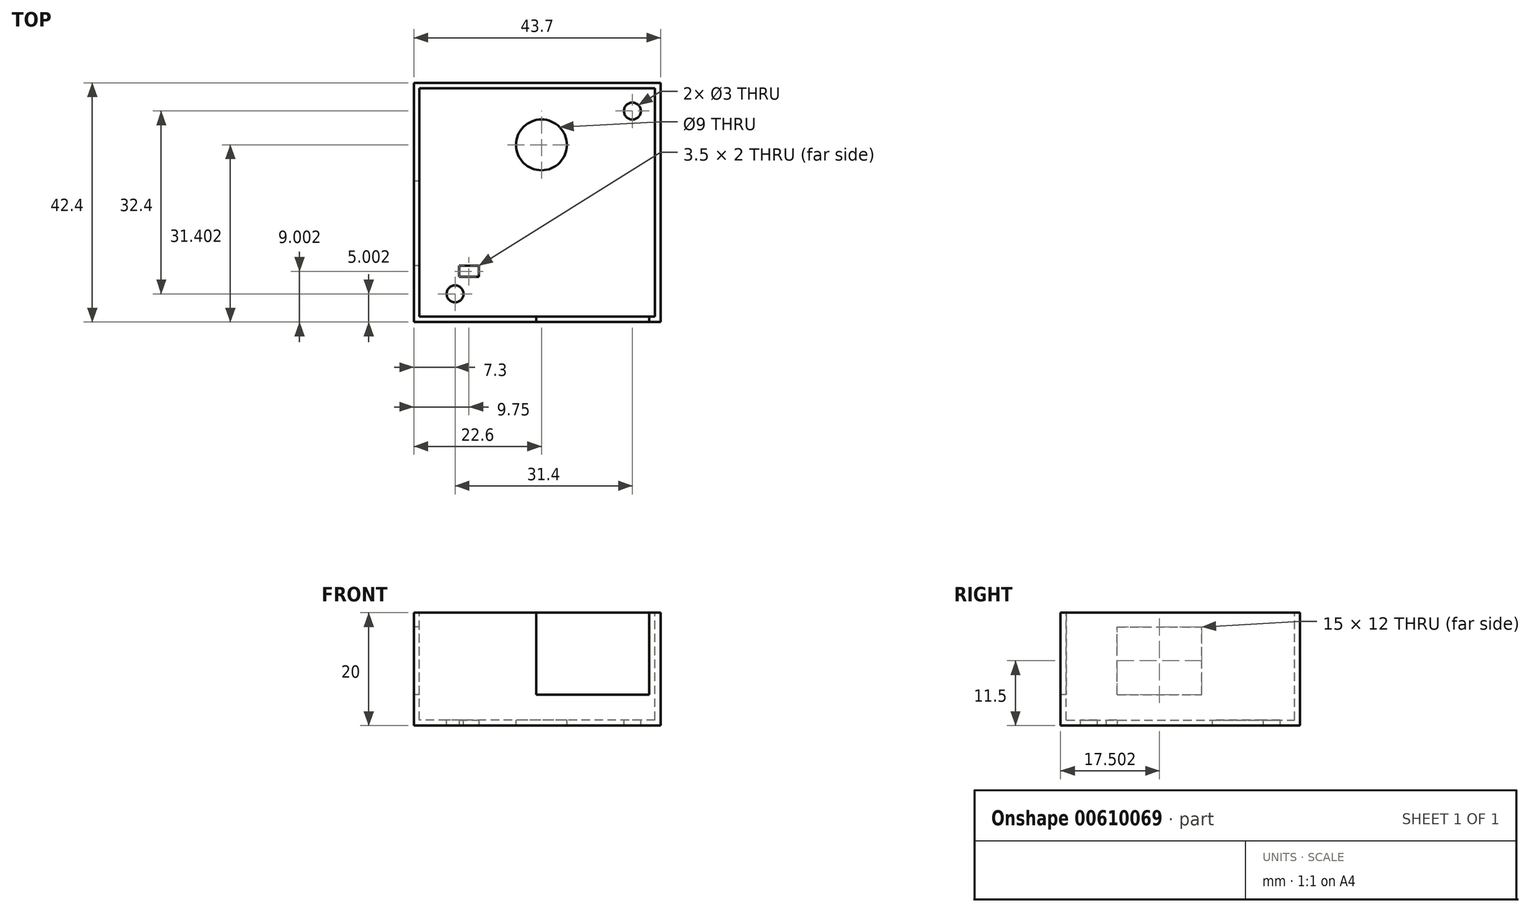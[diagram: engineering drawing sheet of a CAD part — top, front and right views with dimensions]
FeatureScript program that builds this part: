
annotation { "Feature Type Name" : "Feature", "Feature Type Description" : "" }
export const myFeature = defineFeature(function(context is Context, id is Id, definition is map)
    precondition{}
    {
        {
            var Q0;
            Q0=qCreatedBy(makeId("Top.planeOp"),FACE);
            var sketch = newSketch(context, id + "F0", { "sketchPlane" : qUnion([Q0])});
            skLineSegment(sketch, "E0.bottom", {"start": v(-43.7, 47.21) * mm, "end": v(0, 47.21) * mm});
            skLineSegment(sketch, "E0.top", {"start": v(-43.7, 4.81) * mm, "end": v(0, 4.81) * mm});
            skLineSegment(sketch, "E0.left", {"start": v(-43.7, 47.21) * mm, "end": v(-43.7, 4.81) * mm});
            skLineSegment(sketch, "E0.right", {"start": v(0, 47.21) * mm, "end": v(0, 4.81) * mm});
            skSolve(sketch);
        }
        {
            var Q0;
            Q0=makeQuery(id+"F0.imprint","IMPRINT",FACE,{"disambiguationData":[TD([[makeQuery(id+"F0.imprint","IMPRINT",EDGE,{"derivedFrom":sQuery(id+"F0.wireOp",EDGE,"E0.bottom")}),-1.0]])]});
            extrude(context, id + "F1", {"entities" : qUnion([Q0]), "depth" : 20 * mm, "offsetDistance" : 25 * mm});
        }
        {
            var Q0;
            Q0=makeQuery(id+"F1.opExtrude","CAP_FACE",FACE,{"disambiguationData":[OSD([sQuery(id+"F0.wireOp",EDGE,"E0.bottom"),sQuery(id+"F0.wireOp",EDGE,"E0.top"),sQuery(id+"F0.wireOp",EDGE,"E0.left"),sQuery(id+"F0.wireOp",EDGE,"E0.right")])],"isStart":false});
            var sketch = newSketch(context, id + "F2", { "sketchPlane" : qUnion([Q0])});
            skLineSegment(sketch, "E1.bottom", {"start": v(-1, 5.81) * mm, "end": v(-42.7, 5.81) * mm});
            skLineSegment(sketch, "E1.top", {"start": v(-1, 46.21) * mm, "end": v(-42.7, 46.21) * mm});
            skLineSegment(sketch, "E1.left", {"start": v(-1, 5.81) * mm, "end": v(-1, 46.21) * mm});
            skLineSegment(sketch, "E1.right", {"start": v(-42.7, 5.81) * mm, "end": v(-42.7, 46.21) * mm});
            skPoint(sketch, "E1.middle", {"position": v(-21.85, 26.01) * mm});
            skPoint(sketch, "E1.middle.positionSnap0", {"position": v(-43.7, 26.01) * mm});
            skPoint(sketch, "E1.middle.positionSnap1", {"position": v(-21.85, 47.21) * mm});
            skPoint(sketch, "E1.centerSnap0", {"position": v(-43.7, 26.01) * mm});
            skPoint(sketch, "E1.centerSnap1", {"position": v(-21.85, 47.21) * mm});
            skSolve(sketch);
        }
        {
            var Q0;
            Q0=makeQuery(id+"F2.imprint","IMPRINT",FACE,{"disambiguationData":[TD([[makeQuery(id+"F2.imprint","IMPRINT",EDGE,{"derivedFrom":sQuery(id+"F2.wireOp",EDGE,"E1.bottom")}),-1.0]])]});
            extrude(context, id + "F3", {"entities" : qUnion([Q0]), "operationType" : NewBodyOperationType.REMOVE, "oppositeDirection" : true, "depth" : 19 * mm, "offsetDistance" : 25 * mm});
        }
        {
            var Q0;
            Q0=makeQuery(id+"F3.boolean.opBoolean","COPY",FACE,{"derivedFrom":makeQuery(id+"F3.opExtrude","CAP_FACE",FACE,{"disambiguationData":[OSD([sQuery(id+"F2.wireOp",EDGE,"E1.bottom"),sQuery(id+"F2.wireOp",EDGE,"E1.top"),sQuery(id+"F2.wireOp",EDGE,"E1.left"),sQuery(id+"F2.wireOp",EDGE,"E1.right")])],"isStart":false})});
            var sketch = newSketch(context, id + "F4", { "sketchPlane" : qUnion([Q0])});
            skCircle(sketch, "E2", {"center": v(-5, 42.21) * mm, "radius": 1.5 * mm});
            skCircle(sketch, "E3", {"center": v(-36.4, 9.81) * mm, "radius": 1.5 * mm});
            skSolve(sketch);
        }
        {
            var Q0;
            Q0=makeQuery(id+"F4.imprint","IMPRINT",FACE,{"disambiguationData":[TD([[makeQuery(id+"F4.imprint","IMPRINT",EDGE,{"derivedFrom":sQuery(id+"F4.wireOp",EDGE,"E2")}),1.0]])]});
            var Q1;
            Q1=makeQuery(id+"F4.imprint","IMPRINT",FACE,{"disambiguationData":[TD([[makeQuery(id+"F4.imprint","IMPRINT",EDGE,{"derivedFrom":sQuery(id+"F4.wireOp",EDGE,"E3")}),1.0]])]});
            extrude(context, id + "F5", {"entities" : qUnion([Q0, Q1]), "operationType" : NewBodyOperationType.REMOVE, "oppositeDirection" : true, "depth" : 1 * mm, "offsetDistance" : 25 * mm});
        }
        {
            var Q0;
            Q0=makeQuery(id+"F3.boolean.opBoolean","COPY",FACE,{"derivedFrom":makeQuery(id+"F3.opExtrude","CAP_FACE",FACE,{"disambiguationData":[OSD([sQuery(id+"F2.wireOp",EDGE,"E1.bottom"),sQuery(id+"F2.wireOp",EDGE,"E1.top"),sQuery(id+"F2.wireOp",EDGE,"E1.left"),sQuery(id+"F2.wireOp",EDGE,"E1.right")])],"isStart":false})});
            var sketch = newSketch(context, id + "F6", { "sketchPlane" : qUnion([Q0])});
            skCircle(sketch, "E4", {"center": v(-21.1, 36.21) * mm, "radius": 4.5 * mm});
            skSolve(sketch);
        }
        {
            var Q0;
            Q0=makeQuery(id+"F6.imprint","IMPRINT",FACE,{"disambiguationData":[TD([[makeQuery(id+"F6.imprint","IMPRINT",EDGE,{"derivedFrom":sQuery(id+"F6.wireOp",EDGE,"E4")}),1.0]])]});
            extrude(context, id + "F7", {"entities" : qUnion([Q0]), "operationType" : NewBodyOperationType.REMOVE, "oppositeDirection" : true, "depth" : 1 * mm, "offsetDistance" : 25 * mm});
        }
        {
            var Q0;
            Q0=makeQuery(id+"F1.opExtrude","SWEPT_FACE",FACE,{"disambiguationData":[OSD([sQuery(id+"F0.wireOp",EDGE,"E0.left")])]});
            var sketch = newSketch(context, id + "F8", { "sketchPlane" : qUnion([Q0])});
            skLineSegment(sketch, "E5.bottom", {"start": v(-14.81, 5.5) * mm, "end": v(-29.81, 5.5) * mm});
            skLineSegment(sketch, "E5.top", {"start": v(-14.81, 17.5) * mm, "end": v(-29.81, 17.5) * mm});
            skLineSegment(sketch, "E5.left", {"start": v(-14.81, 5.5) * mm, "end": v(-14.81, 17.5) * mm});
            skLineSegment(sketch, "E5.right", {"start": v(-29.81, 5.5) * mm, "end": v(-29.81, 17.5) * mm});
            skPoint(sketch, "E5.middle", {"position": v(-22.31, 11.5) * mm});
            skSolve(sketch);
        }
        {
            var Q0;
            Q0=makeQuery(id+"F8.imprint","IMPRINT",FACE,{"disambiguationData":[TD([[makeQuery(id+"F8.imprint","IMPRINT",EDGE,{"derivedFrom":sQuery(id+"F8.wireOp",EDGE,"E5.bottom")}),-1.0]])]});
            extrude(context, id + "F9", {"entities" : qUnion([Q0]), "operationType" : NewBodyOperationType.REMOVE, "oppositeDirection" : true, "depth" : 1 * mm, "offsetDistance" : 25 * mm});
        }
        {
            var Q0;
            Q0=makeQuery(id+"F1.opExtrude","SWEPT_FACE",FACE,{"disambiguationData":[OSD([sQuery(id+"F0.wireOp",EDGE,"E0.top")])]});
            var sketch = newSketch(context, id + "F10", { "sketchPlane" : qUnion([Q0])});
            skLineSegment(sketch, "E6.bottom", {"start": v(-22, 20) * mm, "end": v(-2, 20) * mm});
            skLineSegment(sketch, "E6.top", {"start": v(-22, 5.5) * mm, "end": v(-2, 5.5) * mm});
            skLineSegment(sketch, "E6.left", {"start": v(-22, 20) * mm, "end": v(-22, 5.5) * mm});
            skLineSegment(sketch, "E6.right", {"start": v(-2, 20) * mm, "end": v(-2, 5.5) * mm});
            skSolve(sketch);
        }
        {
            var Q0;
            Q0=makeQuery(id+"F10.imprint","IMPRINT",FACE,{"disambiguationData":[TD([[makeQuery(id+"F10.imprint","IMPRINT",EDGE,{"derivedFrom":sQuery(id+"F10.wireOp",EDGE,"E6.bottom")}),-1.0]])]});
            extrude(context, id + "F11", {"entities" : qUnion([Q0]), "operationType" : NewBodyOperationType.REMOVE, "oppositeDirection" : true, "depth" : 1 * mm, "offsetDistance" : 25 * mm});
        }
        {
            var Q0;
            Q0=makeQuery(id+"F1.opExtrude","CAP_FACE",FACE,{"disambiguationData":[OSD([sQuery(id+"F0.wireOp",EDGE,"E0.bottom"),sQuery(id+"F0.wireOp",EDGE,"E0.top"),sQuery(id+"F0.wireOp",EDGE,"E0.left"),sQuery(id+"F0.wireOp",EDGE,"E0.right")])],"isStart":true});
            var sketch = newSketch(context, id + "F12", { "sketchPlane" : qUnion([Q0])});
            skLineSegment(sketch, "E7.bottom", {"start": v(-35.7, -14.81) * mm, "end": v(-32.2, -14.81) * mm});
            skLineSegment(sketch, "E7.top", {"start": v(-35.7, -12.81) * mm, "end": v(-32.2, -12.81) * mm});
            skLineSegment(sketch, "E7.left", {"start": v(-35.7, -14.81) * mm, "end": v(-35.7, -12.81) * mm});
            skLineSegment(sketch, "E7.right", {"start": v(-32.2, -14.81) * mm, "end": v(-32.2, -12.81) * mm});
            skSolve(sketch);
        }
        {
            var Q0;
            Q0=makeQuery(id+"F12.imprint","IMPRINT",FACE,{"disambiguationData":[TD([[makeQuery(id+"F12.imprint","IMPRINT",EDGE,{"derivedFrom":sQuery(id+"F12.wireOp",EDGE,"E7.bottom")}),1.0]])]});
            extrude(context, id + "F13", {"entities" : qUnion([Q0]), "operationType" : NewBodyOperationType.REMOVE, "oppositeDirection" : true, "depth" : 1 * mm, "offsetDistance" : 25 * mm});
        }
    });
